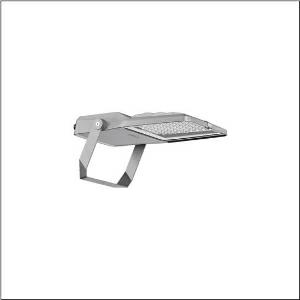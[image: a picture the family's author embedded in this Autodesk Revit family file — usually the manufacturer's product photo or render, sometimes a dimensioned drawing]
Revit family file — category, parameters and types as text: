
# Revit family: floodlight_fl_21_iq_mini___pl61_5xa7772c2c1a_b30e
name_source: partatom
category: Lighting Fixtures
units: mm (PartAtom-declared; Revit-internal decimal feet)

## family parameters
Cut with Voids When Loaded = No
Host = Face
Light Source = No
Part Type = Normal
Room Calculation Point = No
Round Connector Dimension = Use Diameter
Shared = No

## types (1)
- --- (1 x LED, 11980 lm, 87.2 W, 3000K)
    Apparent Load = 87 VA
    CIE Flux Codes = 33 65 98 100 100
    Color Rendering = 70
    Color Temperature = 3000K
    Default Elevation = 1800 mm
    Description = Floodlight FL 21 iQ mini, floodlight, primary light control with lens, of PMMA, primary optical cover: protective disc, of toughened safety glass, transparent, light distribution: PL61, light emission: direct distribution, installation type: surface-mounted, LED, High Power LED, rated luminous flux: 11.980lm, luminous efficacy: 137lm/W, light colour: 730, colour temperature: 3000K, control gear: iQ Street-Remote/DALI, control: Street-Remote, Auto-Match, Temp-Guard, Night-Set, Smart-Wire, Desk-Remote (wireless, voltage-free reading and setting of iQ features in the workshop via application-optimized NFC function/RFID function), optimised constant luminous flux control (CLO 2.0), with terminal, 6-pole, mains connection: 220..240V, AC, 50/60Hz, start of lifetime: 87W, end of service life: 92W, reduction: 40W, luminaire housing, of diecast aluminium, powder-coated, Siteco® metallic grey (DB 702S), corrosivity category C5 mid according to DIN EN ISO 12944, suitable for swimming pools, chlorine-resistant, sealing non-destructively replaceable, mounting bracket, of steel, galvanised, powder-coated, Siteco® metallic grey (DB 702S), protection rating (complete): IP66, insulation class (complete): insulation class II (safety insulation), certification: CE, ENEC, VDE, protection symbol: D, impact resistance: IK08, permissible operating ambient temperature: -40..+40°C, permissible operating ambient temperature for outdoor applications: -40..+50°C, standard: DIN EN 12944, LABS conformity tested according to VDMA 24364:2018-05, packaging unit: 1 piece

Light Distribution: PL61
    Height = 70 mm
    Lamp = 1 x LED
    Lamp Light Flux = 11980 lm
    Lamp Power = 87.2 W
    Lamp count = 1
    Length = 485 mm
    Luminous efficacy = 137 lm/W
    Manufacturer = Siteco
    ModVariant = No
    Model = 5XA7772C2C1A
    Number of Poles = 1
    OnlyDefault = Yes
    Power Factor = 1
    Product Name = Floodlight FL 21 iQ mini | PL61
    Product group = floodlight | pylon annexe
    ProductGroupID = 6200
    Protection Class = Protection class II
    Protection Degree = IP 66
    RLX_Detail_Level = 1
    RLX_Emergency_Light_Flux = 0 lm
    RLX_Emergency_Type = 0
    RLX_Emergency_Type_DB = No
    RlxData = <blob elided: 96497 chars, md5=a0dcc825>
    Socket = socket
    Standby Power = 0 W
    System Light Flux = 11980 lm
    System Power = 87 W
    Type Comments = factory setting: luminous flux: 100 % | dim-lin: 254 | 456 mA
    Type Image = l_1006845.jpg
    URL = http://relux.com
    VarID = @adj_173116
    Voltage = 0 V
    Weight = 0.00 kg
    Width = 337 mm

## geometry (parser evidence)
native form markers: Blend x4, Sweep x10
no freeform markers — native parametric forms only
